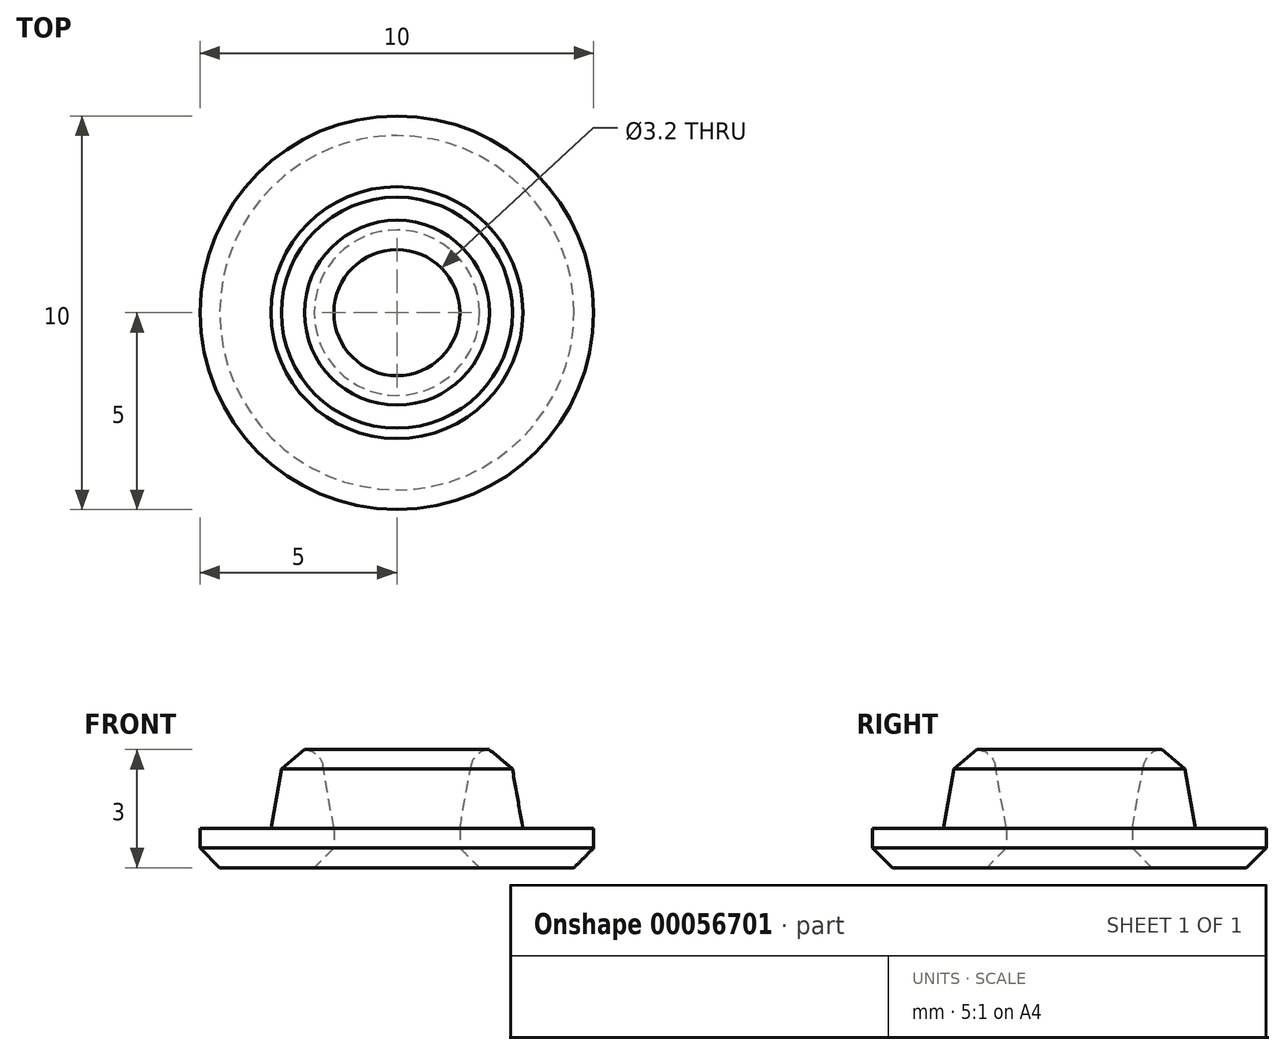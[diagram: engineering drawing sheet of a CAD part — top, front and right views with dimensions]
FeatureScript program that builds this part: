
annotation { "Feature Type Name" : "Feature", "Feature Type Description" : "" }
export const myFeature = defineFeature(function(context is Context, id is Id, definition is map)
    precondition{}
    {
        {
            var Q0;
            Q0=qCreatedBy(makeId("Top.planeOp"),FACE);
            var sketch = newSketch(context, id + "F0", { "sketchPlane" : qUnion([Q0])});
            skCircle(sketch, "E0", {"center": v(0, 0) * mm, "radius": 5 * mm});
            skCircle(sketch, "E1", {"center": v(0, 0) * mm, "radius": 1.6 * mm});
            skSolve(sketch);
        }
        {
            var Q0;
            Q0=makeQuery(id+"F0.imprint","IMPRINT",FACE,{"disambiguationData":[TD([[makeQuery(id+"F0.imprint","IMPRINT",EDGE,{"derivedFrom":sQuery(id+"F0.wireOp",EDGE,"E0")}),1.0]])]});
            extrude(context, id + "F1", {"entities" : qUnion([Q0]), "depth" : 1 * mm});
        }
        {
            var Q0;
            Q0=makeQuery(id+"F1.opExtrude","CAP_FACE",FACE,{"disambiguationData":[OSD([sQuery(id+"F0.wireOp",EDGE,"E0")])],"isStart":false});
            var sketch = newSketch(context, id + "F2", { "sketchPlane" : qUnion([Q0])});
            skCircle(sketch, "E2", {"center": v(0, 0) * mm, "radius": 3.2 * mm});
            skSolve(sketch);
        }
        {
            var Q0;
            Q0=makeQuery(id+"F2.imprint","IMPRINT",FACE,{"disambiguationData":[TD([[makeQuery(id+"F2.imprint","IMPRINT",EDGE,{"derivedFrom":sQuery(id+"F2.wireOp",EDGE,"E2")}),1.0]])]});
            extrude(context, id + "F3", {"entities" : qUnion([Q0]), "operationType" : NewBodyOperationType.ADD, "depth" : 2 * mm, "hasDraft" : true, "draftAngle" : 10 * degree, "draftPullDirection" : true});
        }
        {
            var Q0;
            Q0=makeQuery(id+"F1.opExtrude","CAP_EDGE",EDGE,{"disambiguationData":[OSD([sQuery(id+"F0.wireOp",EDGE,"E0")])],"isStart":true});
            var Q1;
            Q1=makeQuery(id+"F3.opExtrude","CAP_EDGE",EDGE,{"disambiguationData":[OSD([sQuery(id+"F2.wireOp",EDGE,"E2")])],"isStart":false});
            var Q2;
            Q2=makeQuery(id+"F1.opExtrude","CAP_EDGE",EDGE,{"disambiguationData":[OSD([sQuery(id+"F0.wireOp",EDGE,"E1")])],"isStart":true});
            chamfer(context, id + "F4", {"entities" : qUnion([Q0, Q1, Q2]), "width" : 0.5 * mm, "tangentPropagation" : true});
        }
        {
            var Q0;
            Q0=makeQuery(id+"F3.opExtrude","CAP_EDGE",EDGE,{"disambiguationData":[OSD([sQuery(id+"F0.wireOp",EDGE,"E1")])],"isStart":false});
            fillet(context, id + "F5", {"entities" : qUnion([Q0]), "radius" : 0.5 * mm, "tangentPropagation" : true, "allowEdgeOverflow" : false});
        }
    });
